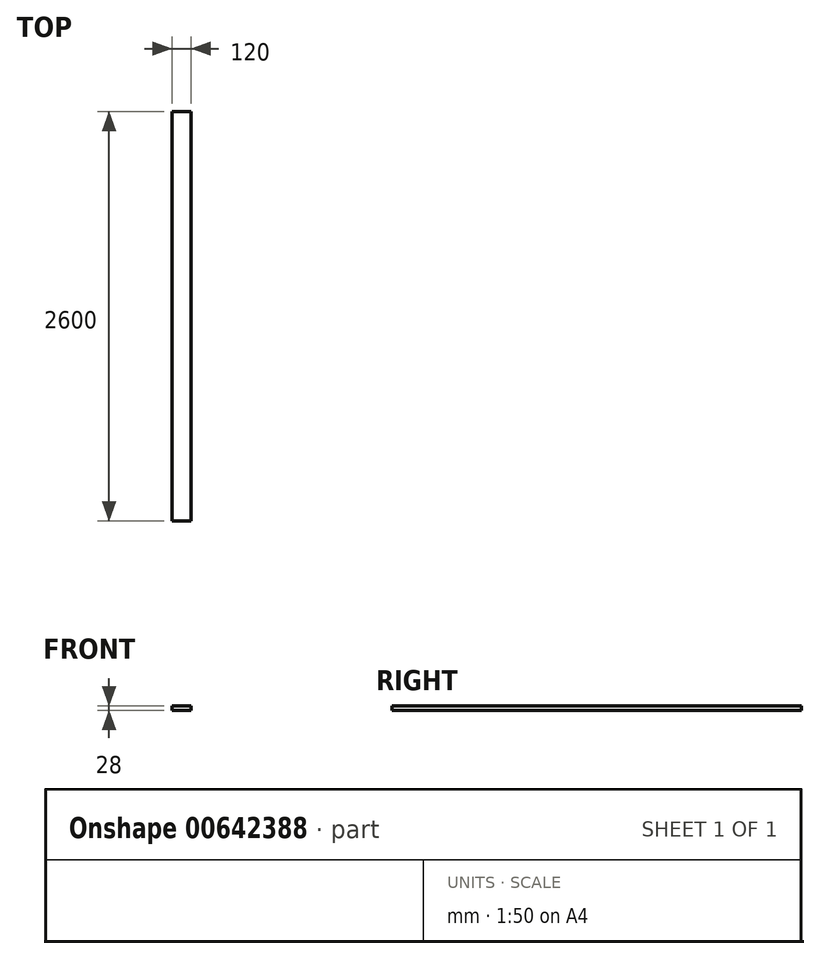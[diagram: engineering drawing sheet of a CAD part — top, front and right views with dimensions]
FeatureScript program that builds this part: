
annotation { "Feature Type Name" : "Feature", "Feature Type Description" : "" }
export const myFeature = defineFeature(function(context is Context, id is Id, definition is map)
    precondition{}
    {
        {
            var Q0;
            Q0=qCreatedBy(makeId("Front.planeOp"),FACE);
            var sketch = newSketch(context, id + "F0", { "sketchPlane" : qUnion([Q0])});
            skLineSegment(sketch, "E0.bottom", {"start": v(0, 0) * mm, "end": v(120, 0) * mm});
            skLineSegment(sketch, "E0.top", {"start": v(0, 28) * mm, "end": v(120, 28) * mm});
            skLineSegment(sketch, "E0.left", {"start": v(0, 0) * mm, "end": v(0, 28) * mm});
            skLineSegment(sketch, "E0.right", {"start": v(120, 0) * mm, "end": v(120, 28) * mm});
            skSolve(sketch);
        }
        {
            var Q0;
            Q0=makeQuery(id+"F0.imprint","IMPRINT",FACE,{"disambiguationData":[TD([[makeQuery(id+"F0.imprint","IMPRINT",EDGE,{"derivedFrom":sQuery(id+"F0.wireOp",EDGE,"E0.bottom")}),1.0]])]});
            extrude(context, id + "F1", {"entities" : qUnion([Q0]), "depth" : 2600 * mm, "offsetDistance" : 25 * mm});
        }
    });
